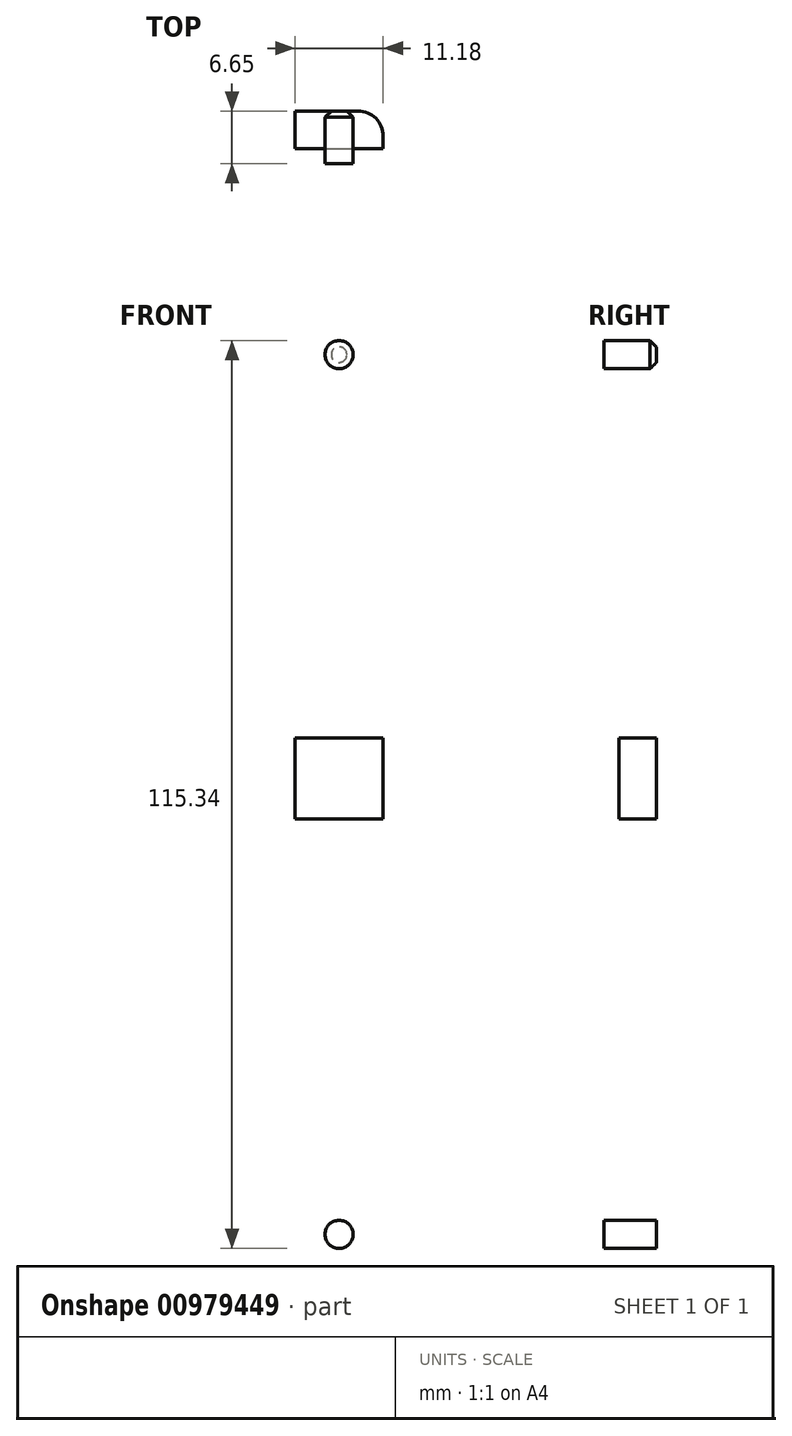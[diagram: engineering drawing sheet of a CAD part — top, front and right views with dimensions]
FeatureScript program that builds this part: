
annotation { "Feature Type Name" : "Feature", "Feature Type Description" : "" }
export const myFeature = defineFeature(function(context is Context, id is Id, definition is map)
    precondition{}
    {
        {
            var Q0;
            Q0=qCreatedBy(makeId("Top.planeOp"),FACE);
            var sketch = newSketch(context, id + "F0", { "sketchPlane" : qUnion([Q0])});
            skLineSegment(sketch, "E0.bottom", {"start": v(62.23, -62.23) * mm, "end": v(-62.23, -62.23) * mm});
            skLineSegment(sketch, "E0.top", {"start": v(62.23, 62.23) * mm, "end": v(-62.23, 62.23) * mm});
            skLineSegment(sketch, "E0.left", {"start": v(62.23, -62.23) * mm, "end": v(62.23, 62.23) * mm});
            skLineSegment(sketch, "E0.right", {"start": v(-62.23, -62.23) * mm, "end": v(-62.23, 62.23) * mm});
            skSolve(sketch);
        }
        {
            var Q0;
            Q0=makeQuery(id+"F0.imprint","IMPRINT",FACE,{"disambiguationData":[TD([[makeQuery(id+"F0.imprint","IMPRINT",EDGE,{"derivedFrom":sQuery(id+"F0.wireOp",EDGE,"E0.bottom")}),-1.0]])]});
            extrude(context, id + "F1", {"entities" : qUnion([Q0]), "depth" : 124.46 * mm, "offsetDistance" : 25.4 * mm});
        }
        {
            var Q0;
            Q0=makeQuery(id+"F1.opExtrude","CAP_FACE",FACE,{"disambiguationData":[OSD([sQuery(id+"F0.wireOp",EDGE,"E0.bottom"),sQuery(id+"F0.wireOp",EDGE,"E0.top"),sQuery(id+"F0.wireOp",EDGE,"E0.left"),sQuery(id+"F0.wireOp",EDGE,"E0.right")])],"isStart":false});
            var sketch = newSketch(context, id + "F2", { "sketchPlane" : qUnion([Q0])});
            skLineSegment(sketch, "E1.bottom", {"start": v(-52.92, 43.18) * mm, "end": v(52.92, 43.18) * mm});
            skLineSegment(sketch, "E1.top", {"start": v(-52.92, -43.18) * mm, "end": v(52.92, -43.18) * mm});
            skLineSegment(sketch, "E1.left", {"start": v(-52.92, 43.18) * mm, "end": v(-52.92, -43.18) * mm});
            skLineSegment(sketch, "E1.right", {"start": v(52.92, 43.18) * mm, "end": v(52.92, -43.18) * mm});
            skPoint(sketch, "E1.middle", {"position": v(0, 0) * mm});
            skCircle(sketch, "E2", {"center": v(-50.38, -40.64) * mm, "radius": 0.76 * mm});
            skCircle(sketch, "E3.MirrorC", {"center": v(50.38, -40.64) * mm, "radius": 0.76 * mm});
            skCircle(sketch, "E4.MirrorC", {"center": v(-50.38, 40.64) * mm, "radius": 0.76 * mm});
            skCircle(sketch, "E5.MirrorC", {"center": v(50.38, 40.64) * mm, "radius": 0.76 * mm});
            skLineSegment(sketch, "E6.0", {"start": v(-53.32, 43.58) * mm, "end": v(-53.32, -43.58) * mm});
            skLineSegment(sketch, "E6.1", {"start": v(-53.32, 43.58) * mm, "end": v(53.32, 43.58) * mm});
            skLineSegment(sketch, "E6.2", {"start": v(53.32, 43.58) * mm, "end": v(53.32, -43.58) * mm});
            skLineSegment(sketch, "E6.3", {"start": v(-53.32, -43.58) * mm, "end": v(53.32, -43.58) * mm});
            skLineSegment(sketch, "E7.top", {"start": v(53.32, -38.1) * mm, "end": v(47.84, -38.1) * mm});
            skLineSegment(sketch, "E7.right", {"start": v(47.84, -43.58) * mm, "end": v(47.84, -38.1) * mm});
            skLineSegment(sketch, "E8.MirrorCS", {"start": v(47.84, 43.58) * mm, "end": v(47.84, 38.1) * mm});
            skLineSegment(sketch, "E9.MirrorCS", {"start": v(53.32, 38.1) * mm, "end": v(47.84, 38.1) * mm});
            skLineSegment(sketch, "E10.MirrorCS", {"start": v(-53.32, -38.1) * mm, "end": v(-47.84, -38.1) * mm});
            skLineSegment(sketch, "E11.MirrorCS", {"start": v(-47.84, -43.58) * mm, "end": v(-47.84, -38.1) * mm});
            skLineSegment(sketch, "E12.MirrorCS", {"start": v(-53.32, 38.1) * mm, "end": v(-47.84, 38.1) * mm});
            skLineSegment(sketch, "E13.MirrorCS", {"start": v(-47.84, 43.58) * mm, "end": v(-47.84, 38.1) * mm});
            skLineSegment(sketch, "E14.MirrorCS", {"start": v(51.04, 6.8) * mm, "end": v(54.8, 6.8) * mm});
            skLineSegment(sketch, "E15.MirrorCS", {"start": v(51.04, -3.13) * mm, "end": v(55.2, -3.13) * mm});
            skLineSegment(sketch, "E16.MirrorCS", {"start": v(51.04, -2.73) * mm, "end": v(54.8, -2.73) * mm});
            skLineSegment(sketch, "E17.MirrorCS", {"start": v(55.2, 7.2) * mm, "end": v(55.2, -3.13) * mm});
            skLineSegment(sketch, "E18.MirrorCS", {"start": v(51.04, 7.2) * mm, "end": v(55.2, 7.2) * mm});
            skLineSegment(sketch, "E19.MirrorCS", {"start": v(54.8, 6.8) * mm, "end": v(54.8, -2.73) * mm});
            skPoint(sketch, "E20.MirrorP", {"position": v(52.92, 2.03) * mm});
            skLineSegment(sketch, "E21.bottom", {"start": v(-62.23, -62.23) * mm, "end": v(62.23, -62.23) * mm});
            skLineSegment(sketch, "E21.top", {"start": v(-62.23, 62.23) * mm, "end": v(62.23, 62.23) * mm});
            skLineSegment(sketch, "E21.left", {"start": v(-62.23, -62.23) * mm, "end": v(-62.23, 62.23) * mm});
            skLineSegment(sketch, "E21.right", {"start": v(62.23, -62.23) * mm, "end": v(62.23, 62.23) * mm});
            skSolve(sketch);
        }
        {
            var Q0;
            Q0=makeQuery(id+"F2.imprint","IMPRINT",FACE,{"disambiguationData":[TD([[makeQuery(id+"F2.imprint","IMPRINT",EDGE,{"derivedFrom":sQuery(id+"F2.wireOp",EDGE,"E2")}),-1.0]])]});
            var Q1;
            {var subQ5=sQuery(id+"F2.wireOp",EDGE,"E1.left");var subQ6=sQuery(id+"F2.wireOp",EDGE,"E1.top");var subQ7=makeQuery(id+"F2.imprint","INTERSECT",VERTEX,{"derivedFrom":[subQ6,subQ5]});Q1=makeQuery(id+"F2.imprint","IMPRINT",FACE,{"disambiguationData":[TD([[makeQuery(id+"F2.imprint","IMPRINT",EDGE,{"disambiguationData":[TD([[subQ7,-1.0]])],"derivedFrom":subQ6}),-1.0]])]});}
            var Q2;
            {var subQ7=sQuery(id+"F2.wireOp",EDGE,"E1.right");var subQ8=sQuery(id+"F2.wireOp",EDGE,"E1.top");var subQ9=makeQuery(id+"F2.imprint","INTERSECT",VERTEX,{"derivedFrom":[subQ8,subQ7]});Q2=makeQuery(id+"F2.imprint","IMPRINT",FACE,{"disambiguationData":[TD([[makeQuery(id+"F2.imprint","IMPRINT",EDGE,{"disambiguationData":[TD([[subQ9,1.0]])],"derivedFrom":subQ8}),-1.0]])]});}
            var Q3;
            Q3=makeQuery(id+"F2.imprint","IMPRINT",FACE,{"disambiguationData":[TD([[makeQuery(id+"F2.imprint","IMPRINT",EDGE,{"derivedFrom":sQuery(id+"F2.wireOp",EDGE,"E3.MirrorC")}),1.0]])]});
            var Q4;
            {var subQ7=sQuery(id+"F2.wireOp",EDGE,"E1.right");var subQ8=sQuery(id+"F2.wireOp",EDGE,"E1.bottom");var subQ9=makeQuery(id+"F2.imprint","INTERSECT",VERTEX,{"derivedFrom":[subQ8,subQ7]});Q4=makeQuery(id+"F2.imprint","IMPRINT",FACE,{"disambiguationData":[TD([[makeQuery(id+"F2.imprint","IMPRINT",EDGE,{"disambiguationData":[TD([[subQ9,1.0]])],"derivedFrom":subQ8}),1.0]])]});}
            var Q5;
            Q5=makeQuery(id+"F2.imprint","IMPRINT",FACE,{"disambiguationData":[TD([[makeQuery(id+"F2.imprint","IMPRINT",EDGE,{"derivedFrom":sQuery(id+"F2.wireOp",EDGE,"E5.MirrorC")}),-1.0]])]});
            var Q6;
            {var subQ5=sQuery(id+"F2.wireOp",EDGE,"E1.left");var subQ6=sQuery(id+"F2.wireOp",EDGE,"E1.bottom");var subQ7=makeQuery(id+"F2.imprint","INTERSECT",VERTEX,{"derivedFrom":[subQ6,subQ5]});Q6=makeQuery(id+"F2.imprint","IMPRINT",FACE,{"disambiguationData":[TD([[makeQuery(id+"F2.imprint","IMPRINT",EDGE,{"disambiguationData":[TD([[subQ7,-1.0]])],"derivedFrom":subQ6}),1.0]])]});}
            var Q7;
            Q7=makeQuery(id+"F2.imprint","IMPRINT",FACE,{"disambiguationData":[TD([[makeQuery(id+"F2.imprint","IMPRINT",EDGE,{"derivedFrom":sQuery(id+"F2.wireOp",EDGE,"E4.MirrorC")}),1.0]])]});
            extrude(context, id + "F3", {"entities" : qUnion([Q0, Q1, Q2, Q3, Q4, Q5, Q6, Q7]), "operationType" : NewBodyOperationType.REMOVE, "oppositeDirection" : true, "depth" : 4.83 * mm, "offsetDistance" : 25.4 * mm});
        }
        {
            var Q0;
            {var subQ20=sQuery(id+"F2.wireOp",EDGE,"E1.bottom");var subQ22=sQuery(id+"F2.wireOp",EDGE,"E13.MirrorCS");var subQ23=makeQuery(id+"F2.imprint","INTERSECT",VERTEX,{"derivedFrom":[subQ20,subQ22]});Q0=makeQuery(id+"F2.imprint","IMPRINT",FACE,{"disambiguationData":[TD([[makeQuery(id+"F2.imprint","IMPRINT",EDGE,{"disambiguationData":[TD([[subQ23,-1.0]])],"derivedFrom":subQ20}),-1.0]])]});}
            var Q1;
            {var subQ0=sQuery(id+"F2.wireOp",EDGE,"E13.MirrorCS");var subQ1=sQuery(id+"F2.wireOp",EDGE,"E1.bottom");var subQ2=makeQuery(id+"F2.imprint","INTERSECT",VERTEX,{"derivedFrom":[subQ1,subQ0]});Q1=makeQuery(id+"F2.imprint","IMPRINT",FACE,{"disambiguationData":[TD([[makeQuery(id+"F2.imprint","IMPRINT",EDGE,{"disambiguationData":[TD([[subQ2,-1.0]])],"derivedFrom":subQ1}),1.0]])]});}
            var Q2;
            {var subQ0=sQuery(id+"F2.wireOp",EDGE,"59694670-6818-448a-b48b-58002c6f26f5.2");var subQ1=sQuery(id+"F2.wireOp",EDGE,"E1.left");var subQ2=makeQuery(id+"F2.imprint","INTERSECT",VERTEX,{"derivedFrom":[subQ1,subQ0]});Q2=makeQuery(id+"F2.imprint","IMPRINT",FACE,{"disambiguationData":[TD([[makeQuery(id+"F2.imprint","IMPRINT",EDGE,{"disambiguationData":[TD([[subQ2,1.0]])],"derivedFrom":subQ1}),-1.0]])]});}
            var Q3;
            {var subQ0=sQuery(id+"F2.wireOp",EDGE,"E9.MirrorCS");var subQ1=sQuery(id+"F2.wireOp",EDGE,"E1.right");var subQ2=makeQuery(id+"F2.imprint","INTERSECT",VERTEX,{"derivedFrom":[subQ1,subQ0]});Q3=makeQuery(id+"F2.imprint","IMPRINT",FACE,{"disambiguationData":[TD([[makeQuery(id+"F2.imprint","IMPRINT",EDGE,{"disambiguationData":[TD([[subQ2,-1.0]])],"derivedFrom":subQ1}),1.0]])]});}
            var Q4;
            {var subQ0=sQuery(id+"F2.wireOp",EDGE,"E11.MirrorCS");var subQ1=sQuery(id+"F2.wireOp",EDGE,"E1.top");var subQ2=makeQuery(id+"F2.imprint","INTERSECT",VERTEX,{"derivedFrom":[subQ1,subQ0]});Q4=makeQuery(id+"F2.imprint","IMPRINT",FACE,{"disambiguationData":[TD([[makeQuery(id+"F2.imprint","IMPRINT",EDGE,{"disambiguationData":[TD([[subQ2,-1.0]])],"derivedFrom":subQ1}),-1.0]])]});}
            var Q5;
            {var subQ0=sQuery(id+"F2.wireOp",EDGE,"01Z94Qzt-EJPi-t4h5-vXe4-wsMJar4ZymQo.bottom");var subQ1=sQuery(id+"F2.wireOp",EDGE,"E1.left");var subQ2=makeQuery(id+"F2.imprint","INTERSECT",VERTEX,{"derivedFrom":[subQ1,subQ0]});Q5=makeQuery(id+"F2.imprint","IMPRINT",FACE,{"disambiguationData":[TD([[makeQuery(id+"F2.imprint","IMPRINT",EDGE,{"disambiguationData":[TD([[subQ2,-1.0]])],"derivedFrom":subQ1}),-1.0]])]});}
            var Q6;
            {var subQ0=sQuery(id+"F2.wireOp",EDGE,"59694670-6818-448a-b48b-58002c6f26f5.2");var subQ1=sQuery(id+"F2.wireOp",EDGE,"E1.left");var subQ2=makeQuery(id+"F2.imprint","INTERSECT",VERTEX,{"derivedFrom":[subQ1,subQ0]});Q6=makeQuery(id+"F2.imprint","IMPRINT",FACE,{"disambiguationData":[TD([[makeQuery(id+"F2.imprint","IMPRINT",EDGE,{"disambiguationData":[TD([[subQ2,-1.0]])],"derivedFrom":subQ1}),-1.0]])]});}
            var Q7;
            {var subQ0=sQuery(id+"F2.wireOp",EDGE,"01Z94Qzt-EJPi-t4h5-vXe4-wsMJar4ZymQo.top");var subQ1=sQuery(id+"F2.wireOp",EDGE,"E1.left");var subQ2=makeQuery(id+"F2.imprint","INTERSECT",VERTEX,{"derivedFrom":[subQ1,subQ0]});Q7=makeQuery(id+"F2.imprint","IMPRINT",FACE,{"disambiguationData":[TD([[makeQuery(id+"F2.imprint","IMPRINT",EDGE,{"disambiguationData":[TD([[subQ2,-1.0]])],"derivedFrom":subQ1}),-1.0]])]});}
            var Q8;
            {var subQ0=sQuery(id+"F2.wireOp",EDGE,"59694670-6818-448a-b48b-58002c6f26f5.0");var subQ1=sQuery(id+"F2.wireOp",EDGE,"E1.left");var subQ2=makeQuery(id+"F2.imprint","INTERSECT",VERTEX,{"derivedFrom":[subQ1,subQ0]});Q8=makeQuery(id+"F2.imprint","IMPRINT",FACE,{"disambiguationData":[TD([[makeQuery(id+"F2.imprint","IMPRINT",EDGE,{"disambiguationData":[TD([[subQ2,-1.0]])],"derivedFrom":subQ1}),-1.0]])]});}
            var Q9;
            {var subQ0=sQuery(id+"F2.wireOp",EDGE,"E18.MirrorCS");var subQ1=sQuery(id+"F2.wireOp",EDGE,"E1.right");var subQ2=makeQuery(id+"F2.imprint","INTERSECT",VERTEX,{"derivedFrom":[subQ1,subQ0]});Q9=makeQuery(id+"F2.imprint","IMPRINT",FACE,{"disambiguationData":[TD([[makeQuery(id+"F2.imprint","IMPRINT",EDGE,{"disambiguationData":[TD([[subQ2,-1.0]])],"derivedFrom":subQ1}),1.0]])]});}
            var Q10;
            {var subQ0=sQuery(id+"F2.wireOp",EDGE,"E14.MirrorCS");var subQ1=sQuery(id+"F2.wireOp",EDGE,"E1.right");var subQ2=makeQuery(id+"F2.imprint","INTERSECT",VERTEX,{"derivedFrom":[subQ1,subQ0]});Q10=makeQuery(id+"F2.imprint","IMPRINT",FACE,{"disambiguationData":[TD([[makeQuery(id+"F2.imprint","IMPRINT",EDGE,{"disambiguationData":[TD([[subQ2,-1.0]])],"derivedFrom":subQ1}),1.0]])]});}
            var Q11;
            {var subQ0=sQuery(id+"F2.wireOp",EDGE,"E16.MirrorCS");var subQ1=sQuery(id+"F2.wireOp",EDGE,"E1.right");var subQ2=makeQuery(id+"F2.imprint","INTERSECT",VERTEX,{"derivedFrom":[subQ1,subQ0]});Q11=makeQuery(id+"F2.imprint","IMPRINT",FACE,{"disambiguationData":[TD([[makeQuery(id+"F2.imprint","IMPRINT",EDGE,{"disambiguationData":[TD([[subQ2,-1.0]])],"derivedFrom":subQ1}),1.0]])]});}
            var Q12;
            {var subQ0=sQuery(id+"F2.wireOp",EDGE,"E15.MirrorCS");var subQ1=sQuery(id+"F2.wireOp",EDGE,"E1.right");var subQ2=makeQuery(id+"F2.imprint","INTERSECT",VERTEX,{"derivedFrom":[subQ1,subQ0]});Q12=makeQuery(id+"F2.imprint","IMPRINT",FACE,{"disambiguationData":[TD([[makeQuery(id+"F2.imprint","IMPRINT",EDGE,{"disambiguationData":[TD([[subQ2,-1.0]])],"derivedFrom":subQ1}),1.0]])]});}
            extrude(context, id + "F4", {"entities" : qUnion([Q0, Q1, Q2, Q3, Q4, Q5, Q6, Q7, Q8, Q9, Q10, Q11, Q12]), "operationType" : NewBodyOperationType.REMOVE, "oppositeDirection" : true, "depth" : 25.4 * mm, "offsetDistance" : 25.4 * mm});
        }
        {
            var Q0;
            Q0=makeQuery(id+"F1.opExtrude","SWEPT_FACE",FACE,{"disambiguationData":[OSD([sQuery(id+"F0.wireOp",EDGE,"E0.bottom")])]});
            var sketch = newSketch(context, id + "F5", { "sketchPlane" : qUnion([Q0])});
            skPoint(sketch, "E22.middle", {"position": v(2.26, 62.23) * mm});
            skCircle(sketch, "E23", {"center": v(-48.12, 21.6) * mm, "radius": 0.76 * mm});
            skCircle(sketch, "E24.MirrorC", {"center": v(52.64, 21.6) * mm, "radius": 0.76 * mm});
            skCircle(sketch, "E25.MirrorC", {"center": v(-48.12, 102.87) * mm, "radius": 0.76 * mm});
            skCircle(sketch, "E26.MirrorC", {"center": v(52.64, 102.87) * mm, "radius": 0.76 * mm});
            skLineSegment(sketch, "E27.0", {"start": v(-51.05, 105.8) * mm, "end": v(-51.05, 18.65) * mm});
            skLineSegment(sketch, "E27.1", {"start": v(-51.05, 105.8) * mm, "end": v(55.58, 105.8) * mm});
            skLineSegment(sketch, "E27.2", {"start": v(55.58, 105.8) * mm, "end": v(55.58, 18.65) * mm});
            skLineSegment(sketch, "E27.3", {"start": v(-51.05, 18.65) * mm, "end": v(55.58, 18.65) * mm});
            skLineSegment(sketch, "E28.top", {"start": v(55.58, 24.13) * mm, "end": v(50.1, 24.13) * mm});
            skLineSegment(sketch, "E28.right", {"start": v(50.1, 18.65) * mm, "end": v(50.1, 24.13) * mm});
            skLineSegment(sketch, "E29.MirrorCS", {"start": v(50.1, 105.8) * mm, "end": v(50.1, 100.33) * mm});
            skLineSegment(sketch, "E30.MirrorCS", {"start": v(55.58, 100.33) * mm, "end": v(50.1, 100.33) * mm});
            skLineSegment(sketch, "E31.MirrorCS", {"start": v(-51.05, 24.13) * mm, "end": v(-45.58, 24.13) * mm});
            skLineSegment(sketch, "E32.MirrorCS", {"start": v(-45.58, 18.65) * mm, "end": v(-45.58, 24.13) * mm});
            skLineSegment(sketch, "E33.MirrorCS", {"start": v(-51.05, 100.33) * mm, "end": v(-45.58, 100.33) * mm});
            skLineSegment(sketch, "E34.MirrorCS", {"start": v(-45.58, 105.8) * mm, "end": v(-45.58, 100.33) * mm});
            skLineSegment(sketch, "E35.MirrorCS", {"start": v(53.3, 59.1) * mm, "end": v(57.46, 59.1) * mm});
            skLineSegment(sketch, "E36.MirrorCS", {"start": v(57.46, 69.42) * mm, "end": v(57.46, 59.1) * mm});
            skLineSegment(sketch, "E37.MirrorCS", {"start": v(53.3, 69.42) * mm, "end": v(57.46, 69.42) * mm});
            skPoint(sketch, "E38.MirrorP", {"position": v(55.18, 64.26) * mm});
            skPoint(sketch, "E39", {"position": v(-62.23, 62.23) * mm});
            skLineSegment(sketch, "E40.bottom", {"start": v(-62.23, 0) * mm, "end": v(62.23, 0) * mm});
            skLineSegment(sketch, "E40.top", {"start": v(-62.23, 124.46) * mm, "end": v(62.23, 124.46) * mm});
            skLineSegment(sketch, "E40.left", {"start": v(-62.23, 0) * mm, "end": v(-62.23, 124.46) * mm});
            skLineSegment(sketch, "E40.right", {"start": v(59.41, 0) * mm, "end": v(59.41, 124.46) * mm});
            skLineSegment(sketch, "E41.bottom", {"start": v(-62.23, 59.1) * mm, "end": v(-51.05, 59.1) * mm});
            skLineSegment(sketch, "E41.top", {"start": v(-62.23, 69.42) * mm, "end": v(-51.05, 69.42) * mm});
            skLineSegment(sketch, "E41.left", {"start": v(-62.23, 59.1) * mm, "end": v(-62.23, 69.42) * mm});
            skLineSegment(sketch, "E41.right", {"start": v(-51.05, 59.1) * mm, "end": v(-51.05, 69.42) * mm});
            skLineSegment(sketch, "E42", {"start": v(-56.25, 69.42) * mm, "end": v(-56.25, 59.1) * mm});
            skLineSegment(sketch, "E43", {"start": v(-45.58, 24.13) * mm, "end": v(50.1, 24.13) * mm});
            skSolve(sketch);
        }
        {
            var Q0;
            Q0=makeQuery(id+"F1.opExtrude","SWEPT_FACE",FACE,{"disambiguationData":[OSD([sQuery(id+"F0.wireOp",EDGE,"E0.left")])]});
            var sketch = newSketch(context, id + "F6", { "sketchPlane" : qUnion([Q0])});
            skPoint(sketch, "E44.middle", {"position": v(2.26, 62.23) * mm});
            skCircle(sketch, "E45", {"center": v(-48.12, 21.59) * mm, "radius": 0.76 * mm});
            skCircle(sketch, "E46.MirrorC", {"center": v(52.64, 21.59) * mm, "radius": 0.76 * mm});
            skCircle(sketch, "E47.MirrorC", {"center": v(-48.12, 102.87) * mm, "radius": 0.76 * mm});
            skCircle(sketch, "E48.MirrorC", {"center": v(52.64, 102.87) * mm, "radius": 0.76 * mm});
            skLineSegment(sketch, "E49.0", {"start": v(-51.05, 105.8) * mm, "end": v(-51.05, 18.65) * mm});
            skLineSegment(sketch, "E49.1", {"start": v(-51.05, 105.8) * mm, "end": v(55.58, 105.8) * mm});
            skLineSegment(sketch, "E49.2", {"start": v(55.58, 105.8) * mm, "end": v(55.58, 18.65) * mm});
            skLineSegment(sketch, "E49.3", {"start": v(-51.05, 18.65) * mm, "end": v(55.58, 18.65) * mm});
            skLineSegment(sketch, "E50.top", {"start": v(55.58, 24.13) * mm, "end": v(50.1, 24.13) * mm});
            skLineSegment(sketch, "E50.right", {"start": v(50.1, 18.65) * mm, "end": v(50.1, 24.13) * mm});
            skLineSegment(sketch, "E51.MirrorCS", {"start": v(50.1, 105.8) * mm, "end": v(50.1, 100.33) * mm});
            skLineSegment(sketch, "E52.MirrorCS", {"start": v(55.58, 100.33) * mm, "end": v(50.1, 100.33) * mm});
            skLineSegment(sketch, "E53.MirrorCS", {"start": v(-51.05, 24.13) * mm, "end": v(-45.58, 24.13) * mm});
            skLineSegment(sketch, "E54.MirrorCS", {"start": v(-45.58, 18.65) * mm, "end": v(-45.58, 24.13) * mm});
            skLineSegment(sketch, "E55.MirrorCS", {"start": v(-51.05, 100.33) * mm, "end": v(-45.58, 100.33) * mm});
            skLineSegment(sketch, "E56.MirrorCS", {"start": v(-45.58, 105.8) * mm, "end": v(-45.58, 100.33) * mm});
            skLineSegment(sketch, "E57.MirrorCS", {"start": v(53.3, 59.1) * mm, "end": v(57.46, 59.1) * mm});
            skLineSegment(sketch, "E58.MirrorCS", {"start": v(57.46, 69.42) * mm, "end": v(57.46, 59.1) * mm});
            skLineSegment(sketch, "E59.MirrorCS", {"start": v(53.3, 69.42) * mm, "end": v(57.46, 69.42) * mm});
            skPoint(sketch, "E60.MirrorP", {"position": v(55.18, 64.26) * mm});
            skPoint(sketch, "E61", {"position": v(-62.23, 62.23) * mm});
            skLineSegment(sketch, "E62.bottom", {"start": v(-62.23, 0) * mm, "end": v(62.23, 0) * mm});
            skLineSegment(sketch, "E62.top", {"start": v(-62.23, 124.46) * mm, "end": v(62.23, 124.46) * mm});
            skLineSegment(sketch, "E62.left", {"start": v(-62.23, 0) * mm, "end": v(-62.23, 124.46) * mm});
            skLineSegment(sketch, "E62.right", {"start": v(62.23, 0) * mm, "end": v(62.23, 124.46) * mm});
            skLineSegment(sketch, "E63.bottom", {"start": v(-62.23, 59.1) * mm, "end": v(-51.05, 59.1) * mm});
            skLineSegment(sketch, "E63.top", {"start": v(-62.23, 69.42) * mm, "end": v(-51.05, 69.42) * mm});
            skLineSegment(sketch, "E63.left", {"start": v(-62.23, 59.1) * mm, "end": v(-62.23, 69.42) * mm});
            skLineSegment(sketch, "E63.right", {"start": v(-51.05, 59.1) * mm, "end": v(-51.05, 69.42) * mm});
            skLineSegment(sketch, "E64", {"start": v(-56.25, 69.42) * mm, "end": v(-56.25, 59.1) * mm});
            skPoint(sketch, "E65", {"position": v(-0.1, 124.46) * mm});
            skLineSegment(sketch, "E66.bottom", {"start": v(-3.13, 124.46) * mm, "end": v(-3.13, 113.28) * mm});
            skLineSegment(sketch, "E66.top", {"start": v(7.2, 124.46) * mm, "end": v(7.2, 113.28) * mm});
            skLineSegment(sketch, "E66.left", {"start": v(-3.13, 124.46) * mm, "end": v(7.2, 124.46) * mm});
            skLineSegment(sketch, "E66.right", {"start": v(-3.13, 113.28) * mm, "end": v(7.2, 113.28) * mm});
            skLineSegment(sketch, "E67", {"start": v(7.2, 118.48) * mm, "end": v(-3.13, 118.48) * mm});
            skLineSegment(sketch, "E68", {"start": v(-45.58, 24.13) * mm, "end": v(50.1, 24.13) * mm});
            skSolve(sketch);
        }
        {
            var Q0;
            Q0=makeQuery(id+"F1.opExtrude","SWEPT_FACE",FACE,{"disambiguationData":[OSD([sQuery(id+"F0.wireOp",EDGE,"E0.top")])]});
            var sketch = newSketch(context, id + "F7", { "sketchPlane" : qUnion([Q0])});
            skPoint(sketch, "E69.middle", {"position": v(2.26, 62.23) * mm});
            skCircle(sketch, "E70", {"center": v(-48.12, 21.59) * mm, "radius": 0.76 * mm});
            skCircle(sketch, "E71.MirrorC", {"center": v(52.64, 21.59) * mm, "radius": 0.76 * mm});
            skCircle(sketch, "E72.MirrorC", {"center": v(-48.12, 102.87) * mm, "radius": 0.76 * mm});
            skCircle(sketch, "E73.MirrorC", {"center": v(52.64, 102.87) * mm, "radius": 0.76 * mm});
            skLineSegment(sketch, "E74.0", {"start": v(-51.05, 105.8) * mm, "end": v(-51.05, 18.65) * mm});
            skLineSegment(sketch, "E74.1", {"start": v(-51.05, 105.8) * mm, "end": v(55.58, 105.8) * mm});
            skLineSegment(sketch, "E74.2", {"start": v(55.58, 105.8) * mm, "end": v(55.58, 18.65) * mm});
            skLineSegment(sketch, "E74.3", {"start": v(-51.05, 18.65) * mm, "end": v(55.58, 18.65) * mm});
            skLineSegment(sketch, "E75.top", {"start": v(55.58, 24.13) * mm, "end": v(50.1, 24.13) * mm});
            skLineSegment(sketch, "E75.right", {"start": v(50.1, 18.65) * mm, "end": v(50.1, 24.13) * mm});
            skLineSegment(sketch, "E76.MirrorCS", {"start": v(50.1, 105.8) * mm, "end": v(50.1, 100.33) * mm});
            skLineSegment(sketch, "E77.MirrorCS", {"start": v(55.58, 100.33) * mm, "end": v(50.1, 100.33) * mm});
            skLineSegment(sketch, "E78.MirrorCS", {"start": v(-51.05, 24.13) * mm, "end": v(-45.58, 24.13) * mm});
            skLineSegment(sketch, "E79.MirrorCS", {"start": v(-45.58, 18.65) * mm, "end": v(-45.58, 24.13) * mm});
            skLineSegment(sketch, "E80.MirrorCS", {"start": v(-51.05, 100.33) * mm, "end": v(-45.58, 100.33) * mm});
            skLineSegment(sketch, "E81.MirrorCS", {"start": v(-45.58, 105.8) * mm, "end": v(-45.58, 100.33) * mm});
            skLineSegment(sketch, "E82.MirrorCS", {"start": v(53.3, 59.1) * mm, "end": v(57.46, 59.1) * mm});
            skLineSegment(sketch, "E83.MirrorCS", {"start": v(57.46, 69.42) * mm, "end": v(57.46, 59.1) * mm});
            skLineSegment(sketch, "E84.MirrorCS", {"start": v(53.3, 69.42) * mm, "end": v(57.46, 69.42) * mm});
            skPoint(sketch, "E85.MirrorP", {"position": v(55.18, 64.26) * mm});
            skPoint(sketch, "E86", {"position": v(-62.23, 62.23) * mm});
            skLineSegment(sketch, "E87.bottom", {"start": v(-62.23, 0) * mm, "end": v(62.23, 0) * mm});
            skLineSegment(sketch, "E87.top", {"start": v(-62.23, 124.46) * mm, "end": v(62.23, 124.46) * mm});
            skLineSegment(sketch, "E87.left", {"start": v(-62.23, 0) * mm, "end": v(-62.23, 124.46) * mm});
            skLineSegment(sketch, "E87.right", {"start": v(62.23, 0) * mm, "end": v(62.23, 124.46) * mm});
            skLineSegment(sketch, "E88.bottom", {"start": v(-62.23, 59.1) * mm, "end": v(-51.05, 59.1) * mm});
            skLineSegment(sketch, "E88.top", {"start": v(-62.23, 69.42) * mm, "end": v(-51.05, 69.42) * mm});
            skLineSegment(sketch, "E88.left", {"start": v(-62.23, 59.1) * mm, "end": v(-62.23, 69.42) * mm});
            skLineSegment(sketch, "E88.right", {"start": v(-51.05, 59.1) * mm, "end": v(-51.05, 69.42) * mm});
            skLineSegment(sketch, "E89", {"start": v(-56.25, 69.42) * mm, "end": v(-56.25, 59.1) * mm});
            skLineSegment(sketch, "E90", {"start": v(-45.58, 24.13) * mm, "end": v(50.1, 24.13) * mm});
            skLineSegment(sketch, "E91", {"start": v(-56.64, 124.46) * mm, "end": v(-56.64, 0) * mm});
            skCircle(sketch, "E92", {"center": v(-56.64, 118.11) * mm, "radius": 1.79 * mm});
            skCircle(sketch, "E93", {"center": v(-56.64, 6.35) * mm, "radius": 1.79 * mm});
            skSolve(sketch);
        }
        {
            var Q0;
            Q0=makeQuery(id+"F1.opExtrude","SWEPT_FACE",FACE,{"disambiguationData":[OSD([sQuery(id+"F0.wireOp",EDGE,"E0.right")])]});
            var sketch = newSketch(context, id + "F8", { "sketchPlane" : qUnion([Q0])});
            skPoint(sketch, "E94.middle", {"position": v(2.26, 62.23) * mm});
            skCircle(sketch, "E95", {"center": v(-48.12, 21.59) * mm, "radius": 0.76 * mm});
            skCircle(sketch, "E96.MirrorC", {"center": v(52.64, 21.59) * mm, "radius": 0.76 * mm});
            skCircle(sketch, "E97.MirrorC", {"center": v(-48.12, 102.87) * mm, "radius": 0.76 * mm});
            skCircle(sketch, "E98.MirrorC", {"center": v(52.64, 102.87) * mm, "radius": 0.76 * mm});
            skLineSegment(sketch, "E99.0", {"start": v(-51.05, 105.8) * mm, "end": v(-51.05, 18.65) * mm});
            skLineSegment(sketch, "E99.1", {"start": v(-51.05, 105.8) * mm, "end": v(55.58, 105.8) * mm});
            skLineSegment(sketch, "E99.2", {"start": v(55.58, 105.8) * mm, "end": v(55.58, 18.65) * mm});
            skLineSegment(sketch, "E99.3", {"start": v(-51.05, 18.65) * mm, "end": v(55.58, 18.65) * mm});
            skLineSegment(sketch, "E100.top", {"start": v(55.58, 24.13) * mm, "end": v(50.1, 24.13) * mm});
            skLineSegment(sketch, "E100.right", {"start": v(50.1, 18.65) * mm, "end": v(50.1, 24.13) * mm});
            skLineSegment(sketch, "E101.MirrorCS", {"start": v(50.1, 105.8) * mm, "end": v(50.1, 100.33) * mm});
            skLineSegment(sketch, "E102.MirrorCS", {"start": v(55.58, 100.33) * mm, "end": v(50.1, 100.33) * mm});
            skLineSegment(sketch, "E103.MirrorCS", {"start": v(-51.05, 24.13) * mm, "end": v(-45.58, 24.13) * mm});
            skLineSegment(sketch, "E104.MirrorCS", {"start": v(-45.58, 18.65) * mm, "end": v(-45.58, 24.13) * mm});
            skLineSegment(sketch, "E105.MirrorCS", {"start": v(-51.05, 100.33) * mm, "end": v(-45.58, 100.33) * mm});
            skLineSegment(sketch, "E106.MirrorCS", {"start": v(-45.58, 105.8) * mm, "end": v(-45.58, 100.33) * mm});
            skLineSegment(sketch, "E107.MirrorCS", {"start": v(53.3, 59.1) * mm, "end": v(57.46, 59.1) * mm});
            skLineSegment(sketch, "E108.MirrorCS", {"start": v(57.46, 69.42) * mm, "end": v(57.46, 59.1) * mm});
            skLineSegment(sketch, "E109.MirrorCS", {"start": v(53.3, 69.42) * mm, "end": v(57.46, 69.42) * mm});
            skPoint(sketch, "E110.MirrorP", {"position": v(55.18, 64.26) * mm});
            skPoint(sketch, "E111", {"position": v(-62.23, 62.23) * mm});
            skLineSegment(sketch, "E112.bottom", {"start": v(-62.23, 0) * mm, "end": v(62.23, 0) * mm});
            skLineSegment(sketch, "E112.top", {"start": v(-62.23, 124.46) * mm, "end": v(62.23, 124.46) * mm});
            skLineSegment(sketch, "E112.left", {"start": v(-62.23, 0) * mm, "end": v(-62.23, 124.46) * mm});
            skLineSegment(sketch, "E112.right", {"start": v(62.23, 0) * mm, "end": v(62.23, 124.46) * mm});
            skLineSegment(sketch, "E113.bottom", {"start": v(-62.23, 59.1) * mm, "end": v(-51.05, 59.1) * mm});
            skLineSegment(sketch, "E113.top", {"start": v(-62.23, 69.42) * mm, "end": v(-51.05, 69.42) * mm});
            skLineSegment(sketch, "E113.left", {"start": v(-62.23, 59.1) * mm, "end": v(-62.23, 69.42) * mm});
            skLineSegment(sketch, "E113.right", {"start": v(-51.05, 59.1) * mm, "end": v(-51.05, 69.42) * mm});
            skLineSegment(sketch, "E114", {"start": v(-56.25, 69.42) * mm, "end": v(-56.25, 59.1) * mm});
            skLineSegment(sketch, "E115", {"start": v(-45.58, 24.13) * mm, "end": v(50.1, 24.13) * mm});
            skSolve(sketch);
        }
        {
            var Q0;
            {var subQ5=sQuery(id+"F5.wireOp",EDGE,"E28.top");Q0=makeQuery(id+"F5.imprint","IMPRINT",FACE,{"disambiguationData":[TD([[makeQuery(id+"F5.imprint","IMPRINT",EDGE,{"derivedFrom":subQ5}),-1.0]])]});}
            var Q1;
            {var subQ5=sQuery(id+"F5.wireOp",EDGE,"E42");Q1=makeQuery(id+"F5.imprint","IMPRINT",FACE,{"disambiguationData":[TD([[makeQuery(id+"F5.imprint","IMPRINT",EDGE,{"derivedFrom":subQ5}),1.0]])]});}
            extrude(context, id + "F9", {"entities" : qUnion([Q0, Q1]), "operationType" : NewBodyOperationType.REMOVE, "oppositeDirection" : true, "depth" : 76.2 * mm, "offsetDistance" : 25.4 * mm});
        }
        {
            var Q0;
            {var subQ5=sQuery(id+"F8.wireOp",EDGE,"E100.top");Q0=makeQuery(id+"F8.imprint","IMPRINT",FACE,{"disambiguationData":[TD([[makeQuery(id+"F8.imprint","IMPRINT",EDGE,{"derivedFrom":subQ5}),-1.0]])]});}
            var Q1;
            {var subQ5=sQuery(id+"F8.wireOp",EDGE,"E114");Q1=makeQuery(id+"F8.imprint","IMPRINT",FACE,{"disambiguationData":[TD([[makeQuery(id+"F8.imprint","IMPRINT",EDGE,{"derivedFrom":subQ5}),1.0]])]});}
            extrude(context, id + "F10", {"entities" : qUnion([Q0, Q1]), "operationType" : NewBodyOperationType.REMOVE, "oppositeDirection" : true, "depth" : 76.2 * mm, "offsetDistance" : 25.4 * mm});
        }
        {
            var Q0;
            {var subQ2=sQuery(id+"F7.wireOp",EDGE,"E75.top");Q0=makeQuery(id+"F7.imprint","IMPRINT",FACE,{"disambiguationData":[TD([[makeQuery(id+"F7.imprint","IMPRINT",EDGE,{"derivedFrom":subQ2}),-1.0]])]});}
            var Q1;
            {var subQ0=sQuery(id+"F7.wireOp",EDGE,"E88.right");Q1=makeQuery(id+"F7.imprint","IMPRINT",FACE,{"disambiguationData":[TD([[makeQuery(id+"F7.imprint","IMPRINT",EDGE,{"derivedFrom":subQ0}),1.0]])]});}
            extrude(context, id + "F11", {"entities" : qUnion([Q0, Q1]), "operationType" : NewBodyOperationType.REMOVE, "oppositeDirection" : true, "depth" : 76.2 * mm, "offsetDistance" : 25.4 * mm});
        }
        {
            var Q0;
            {var subQ5=sQuery(id+"F6.wireOp",EDGE,"E50.top");Q0=makeQuery(id+"F6.imprint","IMPRINT",FACE,{"disambiguationData":[TD([[makeQuery(id+"F6.imprint","IMPRINT",EDGE,{"derivedFrom":subQ5}),-1.0]])]});}
            var Q1;
            {var subQ5=sQuery(id+"F6.wireOp",EDGE,"E64");Q1=makeQuery(id+"F6.imprint","IMPRINT",FACE,{"disambiguationData":[TD([[makeQuery(id+"F6.imprint","IMPRINT",EDGE,{"derivedFrom":subQ5}),1.0]])]});}
            var Q2;
            {var subQ0=sQuery(id+"F6.wireOp",EDGE,"E66.right");Q2=makeQuery(id+"F6.imprint","IMPRINT",FACE,{"disambiguationData":[TD([[makeQuery(id+"F6.imprint","IMPRINT",EDGE,{"derivedFrom":subQ0}),1.0]])]});}
            extrude(context, id + "F12", {"entities" : qUnion([Q0, Q1, Q2]), "operationType" : NewBodyOperationType.REMOVE, "oppositeDirection" : true, "depth" : 76.2 * mm, "offsetDistance" : 25.4 * mm});
        }
        {
            var Q0;
            Q0=makeQuery(id+"F5.imprint","IMPRINT",FACE,{"disambiguationData":[TD([[makeQuery(id+"F5.imprint","IMPRINT",EDGE,{"derivedFrom":sQuery(id+"F5.wireOp",EDGE,"E23")}),1.0]])]});
            var Q1;
            Q1=makeQuery(id+"F5.imprint","IMPRINT",FACE,{"disambiguationData":[TD([[makeQuery(id+"F5.imprint","IMPRINT",EDGE,{"derivedFrom":sQuery(id+"F5.wireOp",EDGE,"E24.MirrorC")}),-1.0]])]});
            var Q2;
            Q2=makeQuery(id+"F5.imprint","IMPRINT",FACE,{"disambiguationData":[TD([[makeQuery(id+"F5.imprint","IMPRINT",EDGE,{"derivedFrom":sQuery(id+"F5.wireOp",EDGE,"E26.MirrorC")}),1.0]])]});
            var Q3;
            Q3=makeQuery(id+"F5.imprint","IMPRINT",FACE,{"disambiguationData":[TD([[makeQuery(id+"F5.imprint","IMPRINT",EDGE,{"derivedFrom":sQuery(id+"F5.wireOp",EDGE,"E25.MirrorC")}),-1.0]])]});
            extrude(context, id + "F13", {"entities" : qUnion([Q0, Q1, Q2, Q3]), "operationType" : NewBodyOperationType.REMOVE, "oppositeDirection" : true, "depth" : 17.53 * mm, "offsetDistance" : 25.4 * mm});
        }
        {
            var Q0;
            Q0=makeQuery(id+"F6.imprint","IMPRINT",FACE,{"disambiguationData":[TD([[makeQuery(id+"F6.imprint","IMPRINT",EDGE,{"derivedFrom":sQuery(id+"F6.wireOp",EDGE,"E47.MirrorC")}),-1.0]])]});
            var Q1;
            Q1=makeQuery(id+"F6.imprint","IMPRINT",FACE,{"disambiguationData":[TD([[makeQuery(id+"F6.imprint","IMPRINT",EDGE,{"derivedFrom":sQuery(id+"F6.wireOp",EDGE,"E48.MirrorC")}),1.0]])]});
            var Q2;
            Q2=makeQuery(id+"F6.imprint","IMPRINT",FACE,{"disambiguationData":[TD([[makeQuery(id+"F6.imprint","IMPRINT",EDGE,{"derivedFrom":sQuery(id+"F6.wireOp",EDGE,"E46.MirrorC")}),-1.0]])]});
            var Q3;
            Q3=makeQuery(id+"F6.imprint","IMPRINT",FACE,{"disambiguationData":[TD([[makeQuery(id+"F6.imprint","IMPRINT",EDGE,{"derivedFrom":sQuery(id+"F6.wireOp",EDGE,"E45")}),1.0]])]});
            extrude(context, id + "F14", {"entities" : qUnion([Q0, Q1, Q2, Q3]), "operationType" : NewBodyOperationType.REMOVE, "oppositeDirection" : true, "depth" : 17.53 * mm, "offsetDistance" : 25.4 * mm});
        }
        {
            var Q0;
            Q0=makeQuery(id+"F7.imprint","IMPRINT",FACE,{"disambiguationData":[TD([[makeQuery(id+"F7.imprint","IMPRINT",EDGE,{"derivedFrom":sQuery(id+"F7.wireOp",EDGE,"E72.MirrorC")}),-1.0]])]});
            var Q1;
            Q1=makeQuery(id+"F7.imprint","IMPRINT",FACE,{"disambiguationData":[TD([[makeQuery(id+"F7.imprint","IMPRINT",EDGE,{"derivedFrom":sQuery(id+"F7.wireOp",EDGE,"E70")}),1.0]])]});
            var Q2;
            Q2=makeQuery(id+"F7.imprint","IMPRINT",FACE,{"disambiguationData":[TD([[makeQuery(id+"F7.imprint","IMPRINT",EDGE,{"derivedFrom":sQuery(id+"F7.wireOp",EDGE,"E71.MirrorC")}),-1.0]])]});
            var Q3;
            Q3=makeQuery(id+"F7.imprint","IMPRINT",FACE,{"disambiguationData":[TD([[makeQuery(id+"F7.imprint","IMPRINT",EDGE,{"derivedFrom":sQuery(id+"F7.wireOp",EDGE,"E73.MirrorC")}),1.0]])]});
            extrude(context, id + "F15", {"entities" : qUnion([Q0, Q1, Q2, Q3]), "operationType" : NewBodyOperationType.REMOVE, "oppositeDirection" : true, "depth" : 17.53 * mm, "offsetDistance" : 25.4 * mm});
        }
        {
            var Q0;
            Q0=makeQuery(id+"F8.imprint","IMPRINT",FACE,{"disambiguationData":[TD([[makeQuery(id+"F8.imprint","IMPRINT",EDGE,{"derivedFrom":sQuery(id+"F8.wireOp",EDGE,"E97.MirrorC")}),-1.0]])]});
            var Q1;
            Q1=makeQuery(id+"F8.imprint","IMPRINT",FACE,{"disambiguationData":[TD([[makeQuery(id+"F8.imprint","IMPRINT",EDGE,{"derivedFrom":sQuery(id+"F8.wireOp",EDGE,"E95")}),1.0]])]});
            var Q2;
            Q2=makeQuery(id+"F8.imprint","IMPRINT",FACE,{"disambiguationData":[TD([[makeQuery(id+"F8.imprint","IMPRINT",EDGE,{"derivedFrom":sQuery(id+"F8.wireOp",EDGE,"E96.MirrorC")}),-1.0]])]});
            var Q3;
            Q3=makeQuery(id+"F8.imprint","IMPRINT",FACE,{"disambiguationData":[TD([[makeQuery(id+"F8.imprint","IMPRINT",EDGE,{"derivedFrom":sQuery(id+"F8.wireOp",EDGE,"E98.MirrorC")}),1.0]])]});
            extrude(context, id + "F16", {"entities" : qUnion([Q0, Q1, Q2, Q3]), "operationType" : NewBodyOperationType.REMOVE, "oppositeDirection" : true, "depth" : 17.53 * mm, "offsetDistance" : 25.4 * mm});
        }
        {
            var Q0;
            Q0=makeQuery(id+"F2.imprint","IMPRINT",FACE,{"disambiguationData":[TD([[makeQuery(id+"F2.imprint","IMPRINT",EDGE,{"derivedFrom":sQuery(id+"F2.wireOp",EDGE,"E4.MirrorC")}),-1.0]])]});
            var Q1;
            Q1=makeQuery(id+"F2.imprint","IMPRINT",FACE,{"disambiguationData":[TD([[makeQuery(id+"F2.imprint","IMPRINT",EDGE,{"derivedFrom":sQuery(id+"F2.wireOp",EDGE,"E5.MirrorC")}),1.0]])]});
            var Q2;
            Q2=makeQuery(id+"F2.imprint","IMPRINT",FACE,{"disambiguationData":[TD([[makeQuery(id+"F2.imprint","IMPRINT",EDGE,{"derivedFrom":sQuery(id+"F2.wireOp",EDGE,"E3.MirrorC")}),-1.0]])]});
            var Q3;
            Q3=makeQuery(id+"F2.imprint","IMPRINT",FACE,{"disambiguationData":[TD([[makeQuery(id+"F2.imprint","IMPRINT",EDGE,{"derivedFrom":sQuery(id+"F2.wireOp",EDGE,"E2")}),1.0]])]});
            var Q4;
            Q4=sQuery(id+"F2.wireOp",EDGE,"E2");
            var Q5;
            Q5=sQuery(id+"F2.wireOp",EDGE,"E4.MirrorC");
            var Q6;
            Q6=sQuery(id+"F2.wireOp",EDGE,"E3.MirrorC");
            var Q7;
            Q7=sQuery(id+"F2.wireOp",EDGE,"E5.MirrorC");
            extrude(context, id + "F17", {"entities" : qUnion([Q0, Q1, Q2, Q3]), "operationType" : NewBodyOperationType.REMOVE, "surfaceEntities" : qUnion([Q4, Q5, Q6, Q7]), "oppositeDirection" : true, "depth" : 17.53 * mm, "offsetDistance" : 25.4 * mm});
        }
        {
            var Q0;
            Q0=makeQuery(id+"F7.imprint","IMPRINT",FACE,{"disambiguationData":[TD([[makeQuery(id+"F7.imprint","IMPRINT",EDGE,{"derivedFrom":sQuery(id+"F7.wireOp",EDGE,"E71.MirrorC")}),1.0]])]});
            var Q1;
            Q1=makeQuery(id+"F7.imprint","IMPRINT",FACE,{"disambiguationData":[TD([[makeQuery(id+"F7.imprint","IMPRINT",EDGE,{"derivedFrom":sQuery(id+"F7.wireOp",EDGE,"E73.MirrorC")}),-1.0]])]});
            var Q2;
            Q2=makeQuery(id+"F7.imprint","IMPRINT",FACE,{"disambiguationData":[TD([[makeQuery(id+"F7.imprint","IMPRINT",EDGE,{"derivedFrom":sQuery(id+"F7.wireOp",EDGE,"E72.MirrorC")}),1.0]])]});
            var Q3;
            Q3=makeQuery(id+"F7.imprint","IMPRINT",FACE,{"disambiguationData":[TD([[makeQuery(id+"F7.imprint","IMPRINT",EDGE,{"derivedFrom":sQuery(id+"F7.wireOp",EDGE,"E70")}),-1.0]])]});
            extrude(context, id + "F18", {"entities" : qUnion([Q0, Q1, Q2, Q3]), "operationType" : NewBodyOperationType.REMOVE, "oppositeDirection" : true, "depth" : 4.83 * mm, "offsetDistance" : 25.4 * mm});
        }
        {
            var Q0;
            Q0=makeQuery(id+"F8.imprint","IMPRINT",FACE,{"disambiguationData":[TD([[makeQuery(id+"F8.imprint","IMPRINT",EDGE,{"derivedFrom":sQuery(id+"F8.wireOp",EDGE,"E95")}),-1.0]])]});
            var Q1;
            Q1=makeQuery(id+"F8.imprint","IMPRINT",FACE,{"disambiguationData":[TD([[makeQuery(id+"F8.imprint","IMPRINT",EDGE,{"derivedFrom":sQuery(id+"F8.wireOp",EDGE,"E97.MirrorC")}),1.0]])]});
            var Q2;
            Q2=makeQuery(id+"F8.imprint","IMPRINT",FACE,{"disambiguationData":[TD([[makeQuery(id+"F8.imprint","IMPRINT",EDGE,{"derivedFrom":sQuery(id+"F8.wireOp",EDGE,"E98.MirrorC")}),-1.0]])]});
            var Q3;
            Q3=makeQuery(id+"F8.imprint","IMPRINT",FACE,{"disambiguationData":[TD([[makeQuery(id+"F8.imprint","IMPRINT",EDGE,{"derivedFrom":sQuery(id+"F8.wireOp",EDGE,"E96.MirrorC")}),1.0]])]});
            extrude(context, id + "F19", {"entities" : qUnion([Q0, Q1, Q2, Q3]), "operationType" : NewBodyOperationType.REMOVE, "oppositeDirection" : true, "depth" : 4.83 * mm, "offsetDistance" : 25.4 * mm});
        }
        {
            var Q0;
            Q0=makeQuery(id+"F5.imprint","IMPRINT",FACE,{"disambiguationData":[TD([[makeQuery(id+"F5.imprint","IMPRINT",EDGE,{"derivedFrom":sQuery(id+"F5.wireOp",EDGE,"E23")}),-1.0]])]});
            var Q1;
            Q1=makeQuery(id+"F5.imprint","IMPRINT",FACE,{"disambiguationData":[TD([[makeQuery(id+"F5.imprint","IMPRINT",EDGE,{"derivedFrom":sQuery(id+"F5.wireOp",EDGE,"E25.MirrorC")}),1.0]])]});
            var Q2;
            Q2=makeQuery(id+"F5.imprint","IMPRINT",FACE,{"disambiguationData":[TD([[makeQuery(id+"F5.imprint","IMPRINT",EDGE,{"derivedFrom":sQuery(id+"F5.wireOp",EDGE,"E26.MirrorC")}),-1.0]])]});
            var Q3;
            Q3=makeQuery(id+"F5.imprint","IMPRINT",FACE,{"disambiguationData":[TD([[makeQuery(id+"F5.imprint","IMPRINT",EDGE,{"derivedFrom":sQuery(id+"F5.wireOp",EDGE,"E24.MirrorC")}),1.0]])]});
            extrude(context, id + "F20", {"entities" : qUnion([Q0, Q1, Q2, Q3]), "operationType" : NewBodyOperationType.REMOVE, "oppositeDirection" : true, "depth" : 4.83 * mm, "offsetDistance" : 25.4 * mm});
        }
        {
            var Q0;
            Q0=makeQuery(id+"F6.imprint","IMPRINT",FACE,{"disambiguationData":[TD([[makeQuery(id+"F6.imprint","IMPRINT",EDGE,{"derivedFrom":sQuery(id+"F6.wireOp",EDGE,"E45")}),-1.0]])]});
            var Q1;
            Q1=makeQuery(id+"F6.imprint","IMPRINT",FACE,{"disambiguationData":[TD([[makeQuery(id+"F6.imprint","IMPRINT",EDGE,{"derivedFrom":sQuery(id+"F6.wireOp",EDGE,"E47.MirrorC")}),1.0]])]});
            var Q2;
            Q2=makeQuery(id+"F6.imprint","IMPRINT",FACE,{"disambiguationData":[TD([[makeQuery(id+"F6.imprint","IMPRINT",EDGE,{"derivedFrom":sQuery(id+"F6.wireOp",EDGE,"E48.MirrorC")}),-1.0]])]});
            var Q3;
            Q3=makeQuery(id+"F6.imprint","IMPRINT",FACE,{"disambiguationData":[TD([[makeQuery(id+"F6.imprint","IMPRINT",EDGE,{"derivedFrom":sQuery(id+"F6.wireOp",EDGE,"E46.MirrorC")}),1.0]])]});
            extrude(context, id + "F21", {"entities" : qUnion([Q0, Q1, Q2, Q3]), "operationType" : NewBodyOperationType.REMOVE, "oppositeDirection" : true, "depth" : 4.83 * mm, "offsetDistance" : 25.4 * mm});
        }
        {
            var Q0;
            {var subQ5=sQuery(id+"F5.wireOp",EDGE,"E36.MirrorCS");Q0=makeQuery(id+"F5.imprint","IMPRINT",FACE,{"disambiguationData":[TD([[makeQuery(id+"F5.imprint","IMPRINT",EDGE,{"derivedFrom":subQ5}),-1.0]])]});}
            extrude(context, id + "F22", {"entities" : qUnion([Q0]), "operationType" : NewBodyOperationType.REMOVE, "oppositeDirection" : true, "depth" : 11.18 * mm, "offsetDistance" : 25.4 * mm});
        }
        {
            var Q0;
            {var subQ5=sQuery(id+"F6.wireOp",EDGE,"E58.MirrorCS");Q0=makeQuery(id+"F6.imprint","IMPRINT",FACE,{"disambiguationData":[TD([[makeQuery(id+"F6.imprint","IMPRINT",EDGE,{"derivedFrom":subQ5}),-1.0]])]});}
            extrude(context, id + "F23", {"entities" : qUnion([Q0]), "operationType" : NewBodyOperationType.REMOVE, "oppositeDirection" : true, "depth" : 11.18 * mm, "offsetDistance" : 25.4 * mm});
        }
        {
            var Q0;
            {var subQ5=sQuery(id+"F7.wireOp",EDGE,"E83.MirrorCS");Q0=makeQuery(id+"F7.imprint","IMPRINT",FACE,{"disambiguationData":[TD([[makeQuery(id+"F7.imprint","IMPRINT",EDGE,{"derivedFrom":subQ5}),-1.0]])]});}
            extrude(context, id + "F24", {"entities" : qUnion([Q0]), "operationType" : NewBodyOperationType.REMOVE, "oppositeDirection" : true, "depth" : 11.18 * mm, "offsetDistance" : 25.4 * mm});
        }
        {
            var Q0;
            {var subQ5=sQuery(id+"F8.wireOp",EDGE,"E108.MirrorCS");Q0=makeQuery(id+"F8.imprint","IMPRINT",FACE,{"disambiguationData":[TD([[makeQuery(id+"F8.imprint","IMPRINT",EDGE,{"derivedFrom":subQ5}),-1.0]])]});}
            extrude(context, id + "F25", {"entities" : qUnion([Q0]), "operationType" : NewBodyOperationType.REMOVE, "oppositeDirection" : true, "depth" : 11.18 * mm, "offsetDistance" : 25.4 * mm});
        }
        {
            var Q0;
            {var subQ0=sQuery(id+"F2.wireOp",EDGE,"E17.MirrorCS");Q0=makeQuery(id+"F2.imprint","IMPRINT",FACE,{"disambiguationData":[TD([[makeQuery(id+"F2.imprint","IMPRINT",EDGE,{"derivedFrom":subQ0}),-1.0]])]});}
            var Q1;
            {var subQ5=sQuery(id+"F2.wireOp",EDGE,"E19.MirrorCS");Q1=makeQuery(id+"F2.imprint","IMPRINT",FACE,{"disambiguationData":[TD([[makeQuery(id+"F2.imprint","IMPRINT",EDGE,{"derivedFrom":subQ5}),-1.0]])]});}
            extrude(context, id + "F26", {"entities" : qUnion([Q0, Q1]), "operationType" : NewBodyOperationType.REMOVE, "oppositeDirection" : true, "depth" : 11.18 * mm, "offsetDistance" : 25.4 * mm});
        }
        {
            var Q0;
            Q0=makeQuery(id+"F1.opExtrude","CAP_FACE",FACE,{"disambiguationData":[OSD([sQuery(id+"F0.wireOp",EDGE,"E0.bottom"),sQuery(id+"F0.wireOp",EDGE,"E0.top"),sQuery(id+"F0.wireOp",EDGE,"E0.left"),sQuery(id+"F0.wireOp",EDGE,"E0.right")])],"isStart":true});
            var sketch = newSketch(context, id + "F27", { "sketchPlane" : qUnion([Q0])});
            skSolve(sketch);
        }
        {
            var Q0;
            Q0=makeQuery(id+"F27.imprint","IMPRINT",FACE,{"disambiguationData":[TD([[makeQuery(id+"F27.imprint","IMPRINT",EDGE,{"derivedFrom":makeQuery(id+"F1.opExtrude","CAP_EDGE",EDGE,{"disambiguationData":[OSD([sQuery(id+"F0.wireOp",EDGE,"E0.bottom")])],"isStart":true})}),1.0]])]});
            var sketch = newSketch(context, id + "F28", { "sketchPlane" : qUnion([Q0])});
            skLineSegment(sketch, "E116.bottom", {"start": v(-62.23, -62.23) * mm, "end": v(62.23, -62.23) * mm});
            skLineSegment(sketch, "E116.top", {"start": v(-62.23, 62.23) * mm, "end": v(62.23, 62.23) * mm});
            skLineSegment(sketch, "E116.left", {"start": v(-62.23, -62.23) * mm, "end": v(-62.23, 62.23) * mm});
            skLineSegment(sketch, "E116.right", {"start": v(62.23, -62.23) * mm, "end": v(62.23, 62.23) * mm});
            skPoint(sketch, "E116.middle", {"position": v(0, 0) * mm});
            skLineSegment(sketch, "E117.bottom", {"start": v(-62.23, -62.23) * mm, "end": v(-55.58, -62.23) * mm});
            skLineSegment(sketch, "E117.top", {"start": v(-62.23, -51.05) * mm, "end": v(-55.58, -51.05) * mm});
            skLineSegment(sketch, "E117.left", {"start": v(-62.23, -62.23) * mm, "end": v(-62.23, -51.05) * mm});
            skLineSegment(sketch, "E117.right", {"start": v(-55.58, -62.23) * mm, "end": v(-55.58, -51.05) * mm});
            skLineSegment(sketch, "E118.bottom", {"start": v(62.23, -62.23) * mm, "end": v(62.23, -55.58) * mm});
            skLineSegment(sketch, "E118.top", {"start": v(51.05, -62.23) * mm, "end": v(51.05, -55.58) * mm});
            skLineSegment(sketch, "E118.left", {"start": v(62.23, -62.23) * mm, "end": v(51.05, -62.23) * mm});
            skLineSegment(sketch, "E118.right", {"start": v(62.23, -55.58) * mm, "end": v(51.05, -55.58) * mm});
            skLineSegment(sketch, "E119.bottom", {"start": v(62.23, 62.23) * mm, "end": v(55.58, 62.23) * mm});
            skLineSegment(sketch, "E119.top", {"start": v(62.23, 51.05) * mm, "end": v(55.58, 51.05) * mm});
            skLineSegment(sketch, "E119.left", {"start": v(62.23, 62.23) * mm, "end": v(62.23, 51.05) * mm});
            skLineSegment(sketch, "E119.right", {"start": v(55.58, 62.23) * mm, "end": v(55.58, 51.05) * mm});
            skLineSegment(sketch, "E120.bottom", {"start": v(-62.23, 62.23) * mm, "end": v(-62.23, 55.58) * mm});
            skLineSegment(sketch, "E120.top", {"start": v(-51.05, 62.23) * mm, "end": v(-51.05, 55.58) * mm});
            skLineSegment(sketch, "E120.left", {"start": v(-62.23, 62.23) * mm, "end": v(-51.05, 62.23) * mm});
            skLineSegment(sketch, "E120.right", {"start": v(-62.23, 55.58) * mm, "end": v(-51.05, 55.58) * mm});
            skSolve(sketch);
        }
        {
            var Q0;
            {var subQ4=sQuery(id+"F28.wireOp",EDGE,"E117.top");Q0=makeQuery(id+"F28.imprint","IMPRINT",FACE,{"disambiguationData":[TD([[makeQuery(id+"F28.imprint","IMPRINT",EDGE,{"derivedFrom":subQ4}),1.0]])]});}
            var Q1;
            {var subQ4=sQuery(id+"F28.wireOp",EDGE,"E119.top");Q1=makeQuery(id+"F28.imprint","IMPRINT",FACE,{"disambiguationData":[TD([[makeQuery(id+"F28.imprint","IMPRINT",EDGE,{"derivedFrom":subQ4}),-1.0]])]});}
            var Q2;
            {var subQ3=sQuery(id+"F28.wireOp",EDGE,"E120.top");Q2=makeQuery(id+"F28.imprint","IMPRINT",FACE,{"disambiguationData":[TD([[makeQuery(id+"F28.imprint","IMPRINT",EDGE,{"derivedFrom":subQ3}),-1.0]])]});}
            var Q3;
            {var subQ4=sQuery(id+"F28.wireOp",EDGE,"E117.top");Q3=makeQuery(id+"F28.imprint","IMPRINT",FACE,{"disambiguationData":[TD([[makeQuery(id+"F28.imprint","IMPRINT",EDGE,{"derivedFrom":subQ4}),-1.0]])]});}
            extrude(context, id + "F29", {"entities" : qUnion([Q0, Q1, Q2, Q3]), "operationType" : NewBodyOperationType.REMOVE, "oppositeDirection" : true, "depth" : 127 * mm, "offsetDistance" : 25.4 * mm});
        }
        {
            var Q0;
            {var subQ0=sQuery(id+"F7.wireOp",EDGE,"E92");var subQ1=sQuery(id+"F7.wireOp",EDGE,"E91");var subQ2=makeQuery(id+"F7.imprint","INTERSECT",VERTEX,{"disambiguationData":[OD(0.0)],"derivedFrom":[subQ1,subQ0]});Q0=makeQuery(id+"F7.imprint","IMPRINT",FACE,{"disambiguationData":[TD([[makeQuery(id+"F7.imprint","IMPRINT",EDGE,{"disambiguationData":[TD([[subQ2,-1.0]])],"derivedFrom":subQ1}),1.0]])]});}
            var Q1;
            {var subQ0=sQuery(id+"F7.wireOp",EDGE,"E92");var subQ1=sQuery(id+"F7.wireOp",EDGE,"E91");var subQ2=makeQuery(id+"F7.imprint","INTERSECT",VERTEX,{"disambiguationData":[OD(0.0)],"derivedFrom":[subQ1,subQ0]});Q1=makeQuery(id+"F7.imprint","IMPRINT",FACE,{"disambiguationData":[TD([[makeQuery(id+"F7.imprint","IMPRINT",EDGE,{"disambiguationData":[TD([[subQ2,-1.0]])],"derivedFrom":subQ1}),-1.0]])]});}
            var Q2;
            {var subQ0=sQuery(id+"F7.wireOp",EDGE,"E93");var subQ1=sQuery(id+"F7.wireOp",EDGE,"E91");var subQ2=makeQuery(id+"F7.imprint","INTERSECT",VERTEX,{"disambiguationData":[OD(0.0)],"derivedFrom":[subQ1,subQ0]});Q2=makeQuery(id+"F7.imprint","IMPRINT",FACE,{"disambiguationData":[TD([[makeQuery(id+"F7.imprint","IMPRINT",EDGE,{"disambiguationData":[TD([[subQ2,-1.0]])],"derivedFrom":subQ1}),1.0]])]});}
            var Q3;
            {var subQ0=sQuery(id+"F7.wireOp",EDGE,"E93");var subQ1=sQuery(id+"F7.wireOp",EDGE,"E91");var subQ2=makeQuery(id+"F7.imprint","INTERSECT",VERTEX,{"disambiguationData":[OD(0.0)],"derivedFrom":[subQ1,subQ0]});Q3=makeQuery(id+"F7.imprint","IMPRINT",FACE,{"disambiguationData":[TD([[makeQuery(id+"F7.imprint","IMPRINT",EDGE,{"disambiguationData":[TD([[subQ2,-1.0]])],"derivedFrom":subQ1}),-1.0]])]});}
            extrude(context, id + "F30", {"entities" : qUnion([Q0, Q1, Q2, Q3]), "operationType" : NewBodyOperationType.REMOVE, "oppositeDirection" : true, "depth" : 12.7 * mm, "offsetDistance" : 25.4 * mm});
        }
        {
            var Q0;
            {var subQ3=sQuery(id+"F6.wireOp",EDGE,"E52.MirrorCS");var subQ4=sQuery(id+"F6.wireOp",EDGE,"E49.2");Q0=makeQuery(id+"F29.boolean.opBoolean","MERGE",FACE,{"derivedFrom":[makeQuery(id+"F23.boolean.opBoolean","SPLIT",FACE,{"disambiguationData":[TD([makeQuery(id+"F9.boolean.opBoolean","COPY",FACE,{"derivedFrom":makeQuery(id+"F9.opExtrude","SWEPT_FACE",FACE,{"disambiguationData":[OSD([sQuery(id+"F5.wireOp",EDGE,"E27.1")])]})})])],"derivedFrom":makeQuery(id+"F21.boolean.opBoolean","MERGE",FACE,{"derivedFrom":[makeQuery(id+"F12.boolean.opBoolean","COPY",FACE,{"derivedFrom":makeQuery(id+"F12.opExtrude","SWEPT_FACE",FACE,{"disambiguationData":[OSD([subQ4])]})})],"fromTools":[makeQuery(id+"F21.opExtrude","SWEPT_FACE",FACE,{"disambiguationData":[OSD([subQ4]),TDD([makeQuery(id+"F6.imprint","IMPRINT",EDGE,{"disambiguationData":[TD([[makeQuery(id+"F6.imprint","INTERSECT",VERTEX,{"derivedFrom":[subQ4,subQ3]}),1.0]])],"derivedFrom":subQ4})])]}),makeQuery(id+"F21.opExtrude","SWEPT_FACE",FACE,{"disambiguationData":[OSD([subQ4]),TDD([makeQuery(id+"F6.imprint","IMPRINT",EDGE,{"disambiguationData":[TD([[makeQuery(id+"F6.imprint","INTERSECT",VERTEX,{"derivedFrom":[subQ4,sQuery(id+"F6.wireOp",EDGE,"E49.3")]}),1.0]])],"derivedFrom":subQ4})])]})]})})],"fromTools":[makeQuery(id+"F29.opExtrude","SWEPT_FACE",FACE,{"disambiguationData":[OSD([sQuery(id+"F28.wireOp",EDGE,"E118.right")])]})]});}
            var sketch = newSketch(context, id + "F31", { "sketchPlane" : qUnion([Q0])});
            skLineSegment(sketch, "E121.bottom", {"start": v(53.6, 74.5) * mm, "end": v(59.7, 74.5) * mm});
            skLineSegment(sketch, "E121.top", {"start": v(53.6, 86.36) * mm, "end": v(59.7, 86.36) * mm});
            skLineSegment(sketch, "E121.left", {"start": v(53.6, 74.5) * mm, "end": v(53.6, 86.36) * mm});
            skLineSegment(sketch, "E121.right", {"start": v(59.7, 74.5) * mm, "end": v(59.7, 86.36) * mm});
            skSolve(sketch);
        }
        {
            var Q0;
            Q0=makeQuery(id+"F31.imprint","IMPRINT",FACE,{"disambiguationData":[TD([[makeQuery(id+"F31.imprint","IMPRINT",EDGE,{"derivedFrom":sQuery(id+"F31.wireOp",EDGE,"E121.bottom")}),1.0]])]});
            extrude(context, id + "F32", {"entities" : qUnion([Q0]), "operationType" : NewBodyOperationType.REMOVE, "oppositeDirection" : true, "depth" : 0.8 * mm, "offsetDistance" : 25.4 * mm});
        }
        {
            var Q0;
            Q0=makeQuery(id+"F1.opExtrude","CAP_EDGE",EDGE,{"disambiguationData":[OSD([sQuery(id+"F0.wireOp",EDGE,"E0.left")])],"isStart":true});
            var Q1;
            Q1=makeQuery(id+"F1.opExtrude","CAP_EDGE",EDGE,{"disambiguationData":[OSD([sQuery(id+"F0.wireOp",EDGE,"E0.top")])],"isStart":true});
            var Q2;
            Q2=makeQuery(id+"F1.opExtrude","CAP_EDGE",EDGE,{"disambiguationData":[OSD([sQuery(id+"F0.wireOp",EDGE,"E0.left")])],"isStart":false});
            var Q3;
            Q3=makeQuery(id+"F1.opExtrude","CAP_EDGE",EDGE,{"disambiguationData":[OSD([sQuery(id+"F0.wireOp",EDGE,"E0.top")])],"isStart":false});
            var Q4;
            Q4=makeQuery(id+"F1.opExtrude","SWEPT_EDGE",EDGE,{"disambiguationData":[OSD([sQuery(id+"F0.wireOp",EDGE,"E0.top"),sQuery(id+"F0.wireOp",EDGE,"E0.left")])]});
            fillet(context, id + "F33", {"entities" : qUnion([Q0, Q1, Q2, Q3, Q4]), "radius" : 3.17 * mm, "tangentPropagation" : true, "allowEdgeOverflow" : false});
        }
        {
            var Q0;
            Q0=makeQuery(id+"F32.boolean.opBoolean","COPY",FACE,{"derivedFrom":makeQuery(id+"F32.opExtrude","CAP_FACE",FACE,{"disambiguationData":[OSD([sQuery(id+"F31.wireOp",EDGE,"E121.bottom"),sQuery(id+"F31.wireOp",EDGE,"E121.top"),sQuery(id+"F31.wireOp",EDGE,"E121.left"),sQuery(id+"F31.wireOp",EDGE,"E121.right")])],"isStart":false})});
            var Q1;
            {var subQ0=sQuery(id+"F7.wireOp",EDGE,"E74.0");Q1=makeQuery(id+"F29.boolean.opBoolean","MERGE",EDGE,{"derivedFrom":[makeQuery(id+"F12.boolean.opBoolean","INTERSECT",EDGE,{"derivedFrom":[makeQuery(id+"F11.boolean.opBoolean","COPY",FACE,{"derivedFrom":makeQuery(id+"F11.opExtrude","SWEPT_FACE",FACE,{"disambiguationData":[OSD([subQ0]),TDD([makeQuery(id+"F7.imprint","IMPRINT",EDGE,{"disambiguationData":[TD([[makeQuery(id+"F7.imprint","INTERSECT",VERTEX,{"derivedFrom":[subQ0,sQuery(id+"F7.wireOp",EDGE,"E80.MirrorCS")]}),-1.0]])],"derivedFrom":subQ0})])]})}),makeQuery(id+"F12.opExtrude","SWEPT_FACE",FACE,{"disambiguationData":[OSD([sQuery(id+"F6.wireOp",EDGE,"E49.2")])]})]})],"fromTools":[makeQuery(id+"F29.opExtrude","SWEPT_EDGE",EDGE,{"disambiguationData":[OSD([sQuery(id+"F28.wireOp",EDGE,"E118.top"),sQuery(id+"F28.wireOp",EDGE,"E118.right")])]})]});}
            var Q2;
            {var subQ0=sQuery(id+"F6.wireOp",EDGE,"E49.2");Q2=makeQuery(id+"F29.boolean.opBoolean","MERGE",EDGE,{"derivedFrom":[makeQuery(id+"F23.boolean.opBoolean","SPLIT",EDGE,{"disambiguationData":[TD([makeQuery(id+"F9.boolean.opBoolean","COPY",FACE,{"derivedFrom":makeQuery(id+"F9.opExtrude","SWEPT_FACE",FACE,{"disambiguationData":[OSD([sQuery(id+"F5.wireOp",EDGE,"E27.1")])]})})])],"derivedFrom":makeQuery(id+"F21.boolean.opBoolean","MERGE",EDGE,{"derivedFrom":[makeQuery(id+"F12.boolean.opBoolean","COPY",EDGE,{"derivedFrom":makeQuery(id+"F12.opExtrude","CAP_EDGE",EDGE,{"disambiguationData":[OSD([subQ0])],"isStart":true})})],"fromTools":[makeQuery(id+"F21.opExtrude","CAP_EDGE",EDGE,{"disambiguationData":[OSD([subQ0]),TDD([makeQuery(id+"F6.imprint","IMPRINT",EDGE,{"disambiguationData":[TD([[makeQuery(id+"F6.imprint","INTERSECT",VERTEX,{"derivedFrom":[subQ0,sQuery(id+"F6.wireOp",EDGE,"E52.MirrorCS")]}),1.0]])],"derivedFrom":subQ0})])],"isStart":true}),makeQuery(id+"F21.opExtrude","CAP_EDGE",EDGE,{"disambiguationData":[OSD([subQ0]),TDD([makeQuery(id+"F6.imprint","IMPRINT",EDGE,{"disambiguationData":[TD([[makeQuery(id+"F6.imprint","INTERSECT",VERTEX,{"derivedFrom":[subQ0,sQuery(id+"F6.wireOp",EDGE,"E49.3")]}),1.0]])],"derivedFrom":subQ0})])],"isStart":true})]})})],"fromTools":[makeQuery(id+"F29.opExtrude","SWEPT_EDGE",EDGE,{"disambiguationData":[OSD([sQuery(id+"F28.wireOp",EDGE,"E116.right"),sQuery(id+"F28.wireOp",EDGE,"E118.right")])]})]});}
            var Q3;
            {var subQ0=sQuery(id+"F7.wireOp",EDGE,"E74.0");var subQ1=makeQuery(id+"F7.imprint","INTERSECT",VERTEX,{"derivedFrom":[subQ0,sQuery(id+"F7.wireOp",EDGE,"E80.MirrorCS")]});Q3=makeQuery(id+"F29.boolean.opBoolean","MERGE",EDGE,{"derivedFrom":[makeQuery(id+"F18.boolean.opBoolean","MERGE",EDGE,{"derivedFrom":[makeQuery(id+"F11.boolean.opBoolean","COPY",EDGE,{"derivedFrom":makeQuery(id+"F11.opExtrude","CAP_EDGE",EDGE,{"disambiguationData":[OSD([subQ0]),TDD([makeQuery(id+"F7.imprint","IMPRINT",EDGE,{"disambiguationData":[TD([[subQ1,-1.0]])],"derivedFrom":subQ0})])],"isStart":true})})],"fromTools":[makeQuery(id+"F18.opExtrude","CAP_EDGE",EDGE,{"disambiguationData":[OSD([subQ0]),TDD([makeQuery(id+"F7.imprint","IMPRINT",EDGE,{"disambiguationData":[TD([[makeQuery(id+"F7.imprint","INTERSECT",VERTEX,{"derivedFrom":[subQ0,sQuery(id+"F7.wireOp",EDGE,"E74.1")]}),-1.0]])],"derivedFrom":subQ0})])],"isStart":true})]})],"fromTools":[makeQuery(id+"F29.opExtrude","SWEPT_EDGE",EDGE,{"disambiguationData":[OSD([sQuery(id+"F28.wireOp",EDGE,"E116.bottom"),sQuery(id+"F28.wireOp",EDGE,"E118.top")])]})]});}
            var Q4;
            {var subQ0=sQuery(id+"F7.wireOp",EDGE,"E74.0");var subQ1=makeQuery(id+"F7.imprint","INTERSECT",VERTEX,{"derivedFrom":[subQ0,sQuery(id+"F7.wireOp",EDGE,"E78.MirrorCS")]});Q4=makeQuery(id+"F29.boolean.opBoolean","MERGE",EDGE,{"derivedFrom":[makeQuery(id+"F18.boolean.opBoolean","MERGE",EDGE,{"derivedFrom":[makeQuery(id+"F11.boolean.opBoolean","COPY",EDGE,{"derivedFrom":makeQuery(id+"F11.opExtrude","CAP_EDGE",EDGE,{"disambiguationData":[OSD([subQ0]),TDD([makeQuery(id+"F7.imprint","IMPRINT",EDGE,{"disambiguationData":[TD([[subQ1,1.0]])],"derivedFrom":subQ0})])],"isStart":true})})],"fromTools":[makeQuery(id+"F18.opExtrude","CAP_EDGE",EDGE,{"disambiguationData":[OSD([subQ0]),TDD([makeQuery(id+"F7.imprint","IMPRINT",EDGE,{"disambiguationData":[TD([[makeQuery(id+"F7.imprint","INTERSECT",VERTEX,{"derivedFrom":[subQ0,sQuery(id+"F7.wireOp",EDGE,"E74.3")]}),1.0]])],"derivedFrom":subQ0})])],"isStart":true})]})],"fromTools":[makeQuery(id+"F29.opExtrude","SWEPT_EDGE",EDGE,{"disambiguationData":[OSD([sQuery(id+"F28.wireOp",EDGE,"E116.bottom"),sQuery(id+"F28.wireOp",EDGE,"E118.top")])]})]});}
            var Q5;
            {var subQ0=sQuery(id+"F7.wireOp",EDGE,"E74.0");Q5=makeQuery(id+"F29.boolean.opBoolean","MERGE",EDGE,{"derivedFrom":[makeQuery(id+"F12.boolean.opBoolean","INTERSECT",EDGE,{"derivedFrom":[makeQuery(id+"F11.boolean.opBoolean","COPY",FACE,{"derivedFrom":makeQuery(id+"F11.opExtrude","SWEPT_FACE",FACE,{"disambiguationData":[OSD([subQ0]),TDD([makeQuery(id+"F7.imprint","IMPRINT",EDGE,{"disambiguationData":[TD([[makeQuery(id+"F7.imprint","INTERSECT",VERTEX,{"derivedFrom":[subQ0,sQuery(id+"F7.wireOp",EDGE,"E78.MirrorCS")]}),1.0]])],"derivedFrom":subQ0})])]})}),makeQuery(id+"F12.opExtrude","SWEPT_FACE",FACE,{"disambiguationData":[OSD([sQuery(id+"F6.wireOp",EDGE,"E49.2")])]})]})],"fromTools":[makeQuery(id+"F29.opExtrude","SWEPT_EDGE",EDGE,{"disambiguationData":[OSD([sQuery(id+"F28.wireOp",EDGE,"E118.top"),sQuery(id+"F28.wireOp",EDGE,"E118.right")])]})]});}
            var Q6;
            Q6=makeQuery(id+"F30.boolean.opBoolean","COPY",EDGE,{"derivedFrom":makeQuery(id+"F30.opExtrude","CAP_EDGE",EDGE,{"disambiguationData":[OSD([sQuery(id+"F7.wireOp",EDGE,"E92")])],"isStart":true})});
            var Q7;
            Q7=makeQuery(id+"F30.boolean.opBoolean","COPY",EDGE,{"derivedFrom":makeQuery(id+"F30.opExtrude","CAP_EDGE",EDGE,{"disambiguationData":[OSD([sQuery(id+"F7.wireOp",EDGE,"E93")])],"isStart":true})});
            var Q8;
            {var subQ0=sQuery(id+"F6.wireOp",EDGE,"E49.2");var subQ1=sQuery(id+"F6.wireOp",EDGE,"E49.3");var subQ2=makeQuery(id+"F6.imprint","INTERSECT",VERTEX,{"derivedFrom":[subQ0,subQ1]});Q8=makeQuery(id+"F29.boolean.opBoolean","MERGE",EDGE,{"derivedFrom":[makeQuery(id+"F23.boolean.opBoolean","SPLIT",EDGE,{"disambiguationData":[TD([makeQuery(id+"F11.boolean.opBoolean","COPY",FACE,{"derivedFrom":makeQuery(id+"F11.opExtrude","SWEPT_FACE",FACE,{"disambiguationData":[OSD([sQuery(id+"F7.wireOp",EDGE,"E88.bottom")])]})})])],"derivedFrom":makeQuery(id+"F21.boolean.opBoolean","MERGE",EDGE,{"derivedFrom":[makeQuery(id+"F12.boolean.opBoolean","COPY",EDGE,{"derivedFrom":makeQuery(id+"F12.opExtrude","CAP_EDGE",EDGE,{"disambiguationData":[OSD([subQ0])],"isStart":true})})],"fromTools":[makeQuery(id+"F21.opExtrude","CAP_EDGE",EDGE,{"disambiguationData":[OSD([subQ0]),TDD([makeQuery(id+"F6.imprint","IMPRINT",EDGE,{"disambiguationData":[TD([[makeQuery(id+"F6.imprint","INTERSECT",VERTEX,{"derivedFrom":[subQ0,sQuery(id+"F6.wireOp",EDGE,"E52.MirrorCS")]}),1.0]])],"derivedFrom":subQ0})])],"isStart":true}),makeQuery(id+"F21.opExtrude","CAP_EDGE",EDGE,{"disambiguationData":[OSD([subQ0]),TDD([makeQuery(id+"F6.imprint","IMPRINT",EDGE,{"disambiguationData":[TD([[subQ2,1.0]])],"derivedFrom":subQ0})])],"isStart":true})]})})],"fromTools":[makeQuery(id+"F29.opExtrude","SWEPT_EDGE",EDGE,{"disambiguationData":[OSD([sQuery(id+"F28.wireOp",EDGE,"E116.right"),sQuery(id+"F28.wireOp",EDGE,"E118.right")])]})]});}
            var Q9;
            Q9=makeQuery(id+"F23.boolean.opBoolean","COPY",EDGE,{"derivedFrom":makeQuery(id+"F23.opExtrude","CAP_EDGE",EDGE,{"disambiguationData":[OSD([sQuery(id+"F6.wireOp",EDGE,"E58.MirrorCS")])],"isStart":true})});
            var Q10;
            Q10=makeQuery(id+"F23.boolean.opBoolean","INTERSECT",EDGE,{"derivedFrom":[makeQuery(id+"F11.boolean.opBoolean","COPY",FACE,{"derivedFrom":makeQuery(id+"F11.opExtrude","SWEPT_FACE",FACE,{"disambiguationData":[OSD([sQuery(id+"F7.wireOp",EDGE,"E89")])]})}),makeQuery(id+"F23.opExtrude","SWEPT_FACE",FACE,{"disambiguationData":[OSD([sQuery(id+"F6.wireOp",EDGE,"E58.MirrorCS")])]})]});
            var Q11;
            Q11=makeQuery(id+"F11.boolean.opBoolean","COPY",EDGE,{"derivedFrom":makeQuery(id+"F11.opExtrude","CAP_EDGE",EDGE,{"disambiguationData":[OSD([sQuery(id+"F7.wireOp",EDGE,"E89")])],"isStart":true})});
            var Q12;
            Q12=makeQuery(id+"F11.boolean.opBoolean","COPY",EDGE,{"derivedFrom":makeQuery(id+"F11.opExtrude","SWEPT_EDGE",EDGE,{"disambiguationData":[OSD([sQuery(id+"F7.wireOp",EDGE,"E74.0"),sQuery(id+"F7.wireOp",EDGE,"E88.bottom"),sQuery(id+"F7.wireOp",EDGE,"E88.right")])]})});
            var Q13;
            Q13=makeQuery(id+"F11.boolean.opBoolean","COPY",EDGE,{"derivedFrom":makeQuery(id+"F11.opExtrude","CAP_EDGE",EDGE,{"disambiguationData":[OSD([sQuery(id+"F7.wireOp",EDGE,"E88.bottom")])],"isStart":true})});
            var Q14;
            {var subQ0=sQuery(id+"F6.wireOp",EDGE,"E49.2");Q14=makeQuery(id+"F23.boolean.opBoolean","MERGE",EDGE,{"derivedFrom":[makeQuery(id+"F12.boolean.opBoolean","INTERSECT",EDGE,{"derivedFrom":[makeQuery(id+"F11.boolean.opBoolean","COPY",FACE,{"derivedFrom":makeQuery(id+"F11.opExtrude","SWEPT_FACE",FACE,{"disambiguationData":[OSD([sQuery(id+"F7.wireOp",EDGE,"E88.bottom")])]})}),makeQuery(id+"F12.opExtrude","SWEPT_FACE",FACE,{"disambiguationData":[OSD([subQ0])]})]})],"fromTools":[makeQuery(id+"F23.opExtrude","SWEPT_EDGE",EDGE,{"disambiguationData":[OSD([subQ0,sQuery(id+"F6.wireOp",EDGE,"E57.MirrorCS")])]})]});}
            var Q15;
            Q15=makeQuery(id+"F23.boolean.opBoolean","COPY",EDGE,{"derivedFrom":makeQuery(id+"F23.opExtrude","CAP_EDGE",EDGE,{"disambiguationData":[OSD([sQuery(id+"F6.wireOp",EDGE,"E57.MirrorCS")])],"isStart":true})});
            var Q16;
            {var subQ0=sQuery(id+"F6.wireOp",EDGE,"E49.2");Q16=makeQuery(id+"F23.boolean.opBoolean","MERGE",EDGE,{"derivedFrom":[makeQuery(id+"F12.boolean.opBoolean","INTERSECT",EDGE,{"derivedFrom":[makeQuery(id+"F11.boolean.opBoolean","COPY",FACE,{"derivedFrom":makeQuery(id+"F11.opExtrude","SWEPT_FACE",FACE,{"disambiguationData":[OSD([sQuery(id+"F7.wireOp",EDGE,"E88.top")])]})}),makeQuery(id+"F12.opExtrude","SWEPT_FACE",FACE,{"disambiguationData":[OSD([subQ0])]})]})],"fromTools":[makeQuery(id+"F23.opExtrude","SWEPT_EDGE",EDGE,{"disambiguationData":[OSD([subQ0,sQuery(id+"F6.wireOp",EDGE,"E59.MirrorCS")])]})]});}
            var Q17;
            Q17=makeQuery(id+"F23.boolean.opBoolean","COPY",EDGE,{"derivedFrom":makeQuery(id+"F23.opExtrude","CAP_EDGE",EDGE,{"disambiguationData":[OSD([sQuery(id+"F6.wireOp",EDGE,"E59.MirrorCS")])],"isStart":true})});
            var Q18;
            Q18=makeQuery(id+"F11.boolean.opBoolean","COPY",EDGE,{"derivedFrom":makeQuery(id+"F11.opExtrude","CAP_EDGE",EDGE,{"disambiguationData":[OSD([sQuery(id+"F7.wireOp",EDGE,"E88.top")])],"isStart":true})});
            var Q19;
            Q19=makeQuery(id+"F11.boolean.opBoolean","COPY",EDGE,{"derivedFrom":makeQuery(id+"F11.opExtrude","SWEPT_EDGE",EDGE,{"disambiguationData":[OSD([sQuery(id+"F7.wireOp",EDGE,"E74.0"),sQuery(id+"F7.wireOp",EDGE,"E88.top"),sQuery(id+"F7.wireOp",EDGE,"E88.right")])]})});
            var Q20;
            {var subQ10=sQuery(id+"F0.wireOp",EDGE,"E0.bottom");var subQ14=sQuery(id+"F0.wireOp",EDGE,"E0.right");var subQ16=sQuery(id+"F0.wireOp",EDGE,"E0.top");var subQ18=sQuery(id+"F0.wireOp",EDGE,"E0.left");Q20=makeQuery(id+"F29.boolean.opBoolean","INTERSECT",EDGE,{"derivedFrom":[makeQuery(id+"F3.boolean.opBoolean","SPLIT",FACE,{"disambiguationData":[TD([makeQuery(id+"F1.opExtrude","SWEPT_FACE",FACE,{"disambiguationData":[OSD([subQ10])]})])],"derivedFrom":makeQuery(id+"F1.opExtrude","CAP_FACE",FACE,{"disambiguationData":[OSD([subQ10,subQ16,subQ18,subQ14])],"isStart":false})}),makeQuery(id+"F29.opExtrude","SWEPT_FACE",FACE,{"disambiguationData":[OSD([sQuery(id+"F28.wireOp",EDGE,"E118.top")])]})]});}
            var Q21;
            {var subQ10=sQuery(id+"F0.wireOp",EDGE,"E0.bottom");var subQ14=sQuery(id+"F0.wireOp",EDGE,"E0.right");var subQ16=sQuery(id+"F0.wireOp",EDGE,"E0.top");var subQ18=sQuery(id+"F0.wireOp",EDGE,"E0.left");Q21=makeQuery(id+"F29.boolean.opBoolean","INTERSECT",EDGE,{"derivedFrom":[makeQuery(id+"F3.boolean.opBoolean","SPLIT",FACE,{"disambiguationData":[TD([makeQuery(id+"F1.opExtrude","SWEPT_FACE",FACE,{"disambiguationData":[OSD([subQ10])]})])],"derivedFrom":makeQuery(id+"F1.opExtrude","CAP_FACE",FACE,{"disambiguationData":[OSD([subQ10,subQ16,subQ18,subQ14])],"isStart":false})}),makeQuery(id+"F29.opExtrude","SWEPT_FACE",FACE,{"disambiguationData":[OSD([sQuery(id+"F28.wireOp",EDGE,"E118.right")])]})]});}
            var Q22;
            Q22=makeQuery(id+"F29.boolean.opBoolean","COPY",EDGE,{"derivedFrom":makeQuery(id+"F29.opExtrude","CAP_EDGE",EDGE,{"disambiguationData":[OSD([sQuery(id+"F28.wireOp",EDGE,"E118.top")])],"isStart":true})});
            var Q23;
            Q23=makeQuery(id+"F29.boolean.opBoolean","COPY",EDGE,{"derivedFrom":makeQuery(id+"F29.opExtrude","CAP_EDGE",EDGE,{"disambiguationData":[OSD([sQuery(id+"F28.wireOp",EDGE,"E118.right")])],"isStart":true})});
            chamfer(context, id + "F34", {"entities" : qUnion([Q0, Q1, Q2, Q3, Q4, Q5, Q6, Q7, Q8, Q9, Q10, Q11, Q12, Q13, Q14, Q15, Q16, Q17, Q18, Q19, Q20, Q21, Q22, Q23]), "width" : 0.8 * mm, "tangentPropagation" : true});
        }
    });
